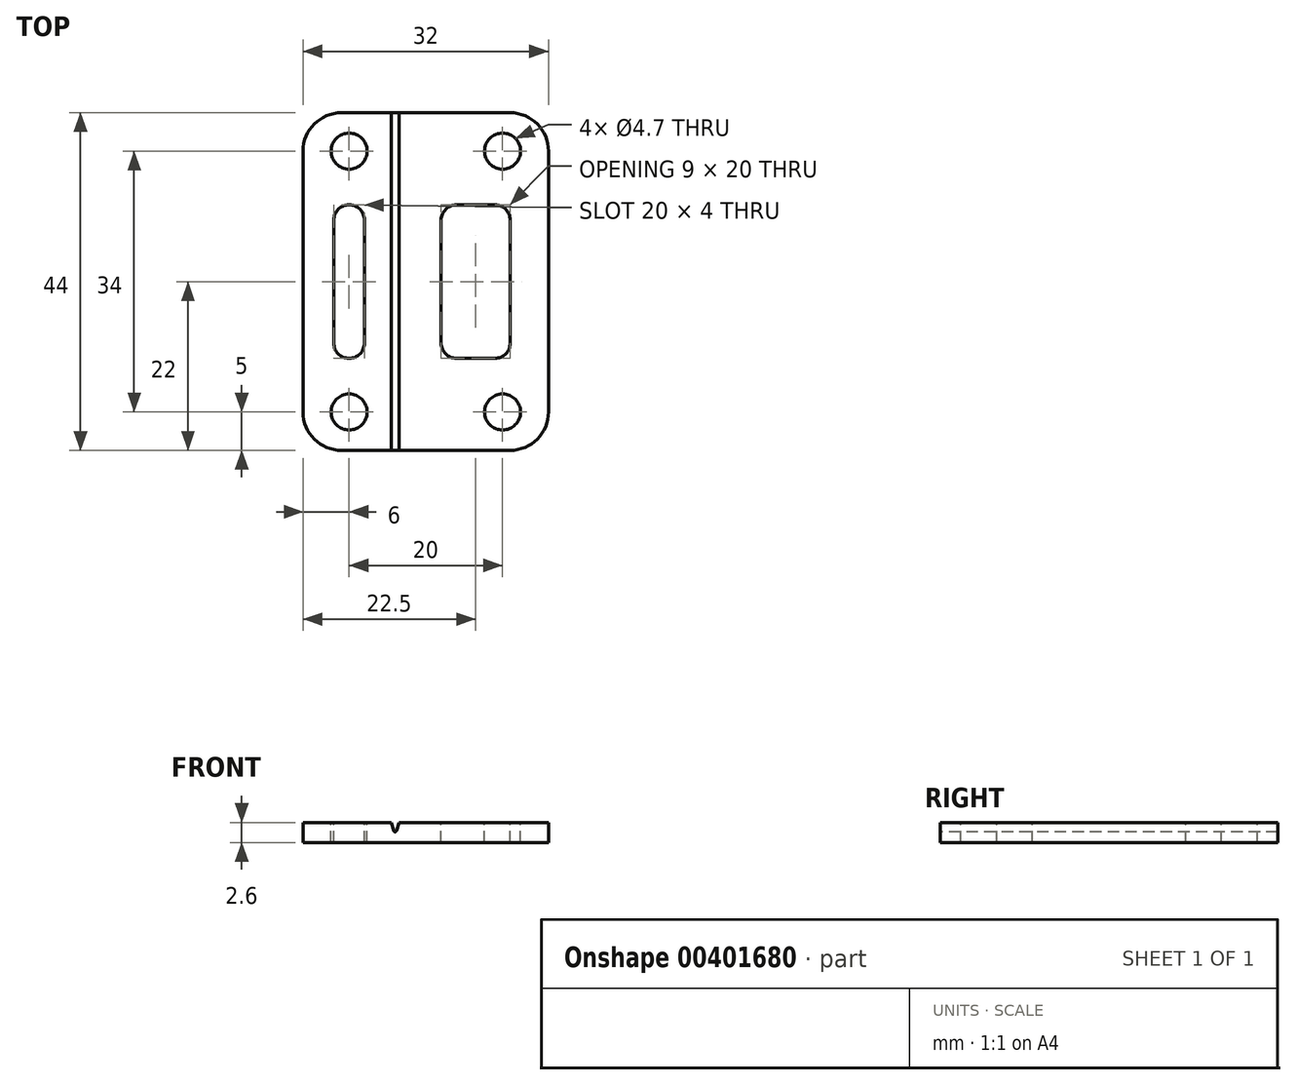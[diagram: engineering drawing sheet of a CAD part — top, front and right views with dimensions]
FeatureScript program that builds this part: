
annotation { "Feature Type Name" : "Feature", "Feature Type Description" : "" }
export const myFeature = defineFeature(function(context is Context, id is Id, definition is map)
    precondition{}
    {
        {
            var Q0;
            Q0=qCreatedBy(makeId("Top.planeOp"),FACE);
            var sketch = newSketch(context, id + "F0", { "sketchPlane" : qUnion([Q0])});
            skLineSegment(sketch, "E0.bottom", {"start": v(0, 0) * mm, "end": v(32, 0) * mm});
            skLineSegment(sketch, "E0.top", {"start": v(0, -44) * mm, "end": v(32, -44) * mm});
            skLineSegment(sketch, "E0.left", {"start": v(0, 0) * mm, "end": v(0, -44) * mm});
            skLineSegment(sketch, "E0.right", {"start": v(32, 0) * mm, "end": v(32, -44) * mm});
            skSolve(sketch);
        }
        {
            var Q0;
            Q0 = qSketchRegion(id + "F0", true);
            extrude(context, id + "F1", {"entities" : qUnion([Q0]), "depth" : 2.6 * mm});
        }
        {
            var Q0;
            Q0=makeQuery(id+"F1.opExtrude","CAP_FACE",FACE,{"disambiguationData":[OSD([sQuery(id+"F0.wireOp",EDGE,"E0.bottom"),sQuery(id+"F0.wireOp",EDGE,"E0.top"),sQuery(id+"F0.wireOp",EDGE,"E0.left"),sQuery(id+"F0.wireOp",EDGE,"E0.right")])],"isStart":false});
            var sketch = newSketch(context, id + "F2", { "sketchPlane" : qUnion([Q0])});
            skCircle(sketch, "E1", {"center": v(6, -5) * mm, "radius": 2.35 * mm});
            skCircle(sketch, "E2", {"center": v(6, -39) * mm, "radius": 2.35 * mm});
            skCircle(sketch, "E3", {"center": v(26, -39) * mm, "radius": 2.35 * mm});
            skCircle(sketch, "E4", {"center": v(26, -5) * mm, "radius": 2.35 * mm});
            skLineSegment(sketch, "E5.bottom", {"start": v(6, -5) * mm, "end": v(26, -5) * mm, "construction": true});
            skLineSegment(sketch, "E5.top", {"start": v(6, -39) * mm, "end": v(26, -39) * mm, "construction": true});
            skLineSegment(sketch, "E5.left", {"start": v(6, -5) * mm, "end": v(6, -39) * mm, "construction": true});
            skLineSegment(sketch, "E5.right", {"start": v(26, -5) * mm, "end": v(26, -39) * mm, "construction": true});
            skLineSegment(sketch, "E6", {"start": v(0, -22) * mm, "end": v(6, -22) * mm, "construction": true});
            skSolve(sketch);
        }
        {
            var Q0;
            Q0 = qSketchRegion(id + "F2", true);
            extrude(context, id + "F3", {"entities" : qUnion([Q0]), "operationType" : NewBodyOperationType.REMOVE, "endBound" : BoundingType.UP_TO_NEXT, "oppositeDirection" : true, "depth" : 25 * mm});
        }
        {
            var Q0;
            Q0=makeQuery(id+"F1.opExtrude","SWEPT_FACE",FACE,{"disambiguationData":[OSD([sQuery(id+"F0.wireOp",EDGE,"E0.top")])]});
            var sketch = newSketch(context, id + "F4", { "sketchPlane" : qUnion([Q0])});
            skLineSegment(sketch, "E7", {"start": v(11.5, 2.6) * mm, "end": v(11.8, 1.54) * mm});
            skLineSegment(sketch, "E8", {"start": v(12.2, 1.54) * mm, "end": v(12.5, 2.6) * mm});
            skLineSegment(sketch, "E9", {"start": v(12.5, 2.6) * mm, "end": v(11.5, 2.6) * mm});
            skPoint(sketch, "E10.visualSharp", {"position": v(12, 0.87) * mm});
            skArc(sketch, "E10.filletArc", {"start": v(11.8, 1.54) * mm, "mid": v(12, 1.4) * mm, "end": v(12.2, 1.54) * mm});
            skLineSegment(sketch, "E11", {"start": v(12, 1.6) * mm, "end": v(12, 1.4) * mm, "construction": true});
            skPoint(sketch, "E11.endSnap0", {"position": v(12, 1.4) * mm});
            skLineSegment(sketch, "E12", {"start": v(12, 1.4) * mm, "end": v(12, 0.87) * mm, "construction": true});
            skLineSegment(sketch, "E13", {"start": v(12, 0.87) * mm, "end": v(12, 0) * mm, "construction": true});
            skSolve(sketch);
        }
        {
            var Q0;
            Q0 = qSketchRegion(id + "F4", true);
            extrude(context, id + "F5", {"entities" : qUnion([Q0]), "operationType" : NewBodyOperationType.REMOVE, "endBound" : BoundingType.THROUGH_ALL, "oppositeDirection" : true, "depth" : 25 * mm});
        }
        {
            var Q0;
            Q0=makeQuery(id+"F1.opExtrude","SWEPT_EDGE",EDGE,{"disambiguationData":[OSD([sQuery(id+"F0.wireOp",EDGE,"E0.top"),sQuery(id+"F0.wireOp",EDGE,"E0.left")])]});
            var Q1;
            Q1=makeQuery(id+"F1.opExtrude","SWEPT_EDGE",EDGE,{"disambiguationData":[OSD([sQuery(id+"F0.wireOp",EDGE,"E0.top"),sQuery(id+"F0.wireOp",EDGE,"E0.right")])]});
            var Q2;
            Q2=makeQuery(id+"F1.opExtrude","SWEPT_EDGE",EDGE,{"disambiguationData":[OSD([sQuery(id+"F0.wireOp",EDGE,"E0.bottom"),sQuery(id+"F0.wireOp",EDGE,"E0.right")])]});
            var Q3;
            Q3=makeQuery(id+"F1.opExtrude","SWEPT_EDGE",EDGE,{"disambiguationData":[OSD([sQuery(id+"F0.wireOp",EDGE,"E0.bottom"),sQuery(id+"F0.wireOp",EDGE,"E0.left")])]});
            fillet(context, id + "F6", {"entities" : qUnion([Q0, Q1, Q2, Q3]), "radius" : 5 * mm, "tangentPropagation" : true, "allowEdgeOverflow" : false});
        }
        {
            var Q0;
            {var subQ0=sQuery(id+"F0.wireOp",EDGE,"E0.left");var subQ1=sQuery(id+"F0.wireOp",EDGE,"E0.top");var subQ2=sQuery(id+"F0.wireOp",EDGE,"E0.bottom");Q0=makeQuery(id+"F5.boolean.opBoolean","SPLIT",FACE,{"disambiguationData":[TD([makeQuery(id+"F1.opExtrude","SWEPT_FACE",FACE,{"disambiguationData":[OSD([subQ0])]})])],"derivedFrom":makeQuery(id+"F1.opExtrude","CAP_FACE",FACE,{"disambiguationData":[OSD([subQ2,subQ1,subQ0,sQuery(id+"F0.wireOp",EDGE,"E0.right")])],"isStart":false})});}
            var sketch = newSketch(context, id + "F7", { "sketchPlane" : qUnion([Q0])});
            skArc(sketch, "E14", {"start": v(8, -14) * mm, "mid": v(6, -12) * mm, "end": v(4, -14) * mm});
            skArc(sketch, "E15", {"start": v(4, -30) * mm, "mid": v(6, -32) * mm, "end": v(8, -30) * mm});
            skLineSegment(sketch, "E16.bottom", {"start": v(18, -12) * mm, "end": v(27, -12) * mm});
            skLineSegment(sketch, "E16.top", {"start": v(18, -32) * mm, "end": v(27, -32) * mm});
            skLineSegment(sketch, "E16.left", {"start": v(18, -12) * mm, "end": v(18, -32) * mm});
            skLineSegment(sketch, "E16.right", {"start": v(27, -12) * mm, "end": v(27, -32) * mm});
            skLineSegment(sketch, "E17", {"start": v(4, -14) * mm, "end": v(4, -30) * mm});
            skLineSegment(sketch, "E18", {"start": v(8, -30) * mm, "end": v(8, -14) * mm});
            skLineSegment(sketch, "E19", {"start": v(6, -12) * mm, "end": v(18, -12) * mm, "construction": true});
            skLineSegment(sketch, "E20", {"start": v(6, -32) * mm, "end": v(18, -32) * mm, "construction": true});
            skLineSegment(sketch, "E21", {"start": v(6, -5) * mm, "end": v(6, -12) * mm, "construction": true});
            skLineSegment(sketch, "E22", {"start": v(0, -22) * mm, "end": v(4, -22) * mm, "construction": true});
            skArc(sketch, "E23", {"start": v(25, -32) * mm, "mid": v(26.41, -31.41) * mm, "end": v(27, -30) * mm});
            skArc(sketch, "E24", {"start": v(27, -14) * mm, "mid": v(26.41, -12.59) * mm, "end": v(25, -12) * mm});
            skArc(sketch, "E25", {"start": v(18, -30) * mm, "mid": v(18.59, -31.41) * mm, "end": v(20, -32) * mm});
            skArc(sketch, "E26.trimOffspring", {"start": v(20, -12) * mm, "mid": v(18.59, -12.59) * mm, "end": v(18, -14) * mm});
            skSolve(sketch);
        }
        {
            var Q0;
            Q0=makeQuery(id+"F7.imprint","IMPRINT",FACE,{"disambiguationData":[TD([[makeQuery(id+"F7.imprint","IMPRINT",EDGE,{"derivedFrom":sQuery(id+"F7.wireOp",EDGE,"E14")}),1.0]])]});
            var Q1;
            {var subQ0=sQuery(id+"F7.wireOp",EDGE,"E23");Q1=makeQuery(id+"F7.imprint","IMPRINT",FACE,{"disambiguationData":[TD([[makeQuery(id+"F7.imprint","IMPRINT",EDGE,{"derivedFrom":subQ0}),1.0]])]});}
            extrude(context, id + "F8", {"entities" : qUnion([Q0, Q1]), "operationType" : NewBodyOperationType.REMOVE, "endBound" : BoundingType.THROUGH_ALL, "oppositeDirection" : true, "depth" : 25 * mm});
        }
    });
